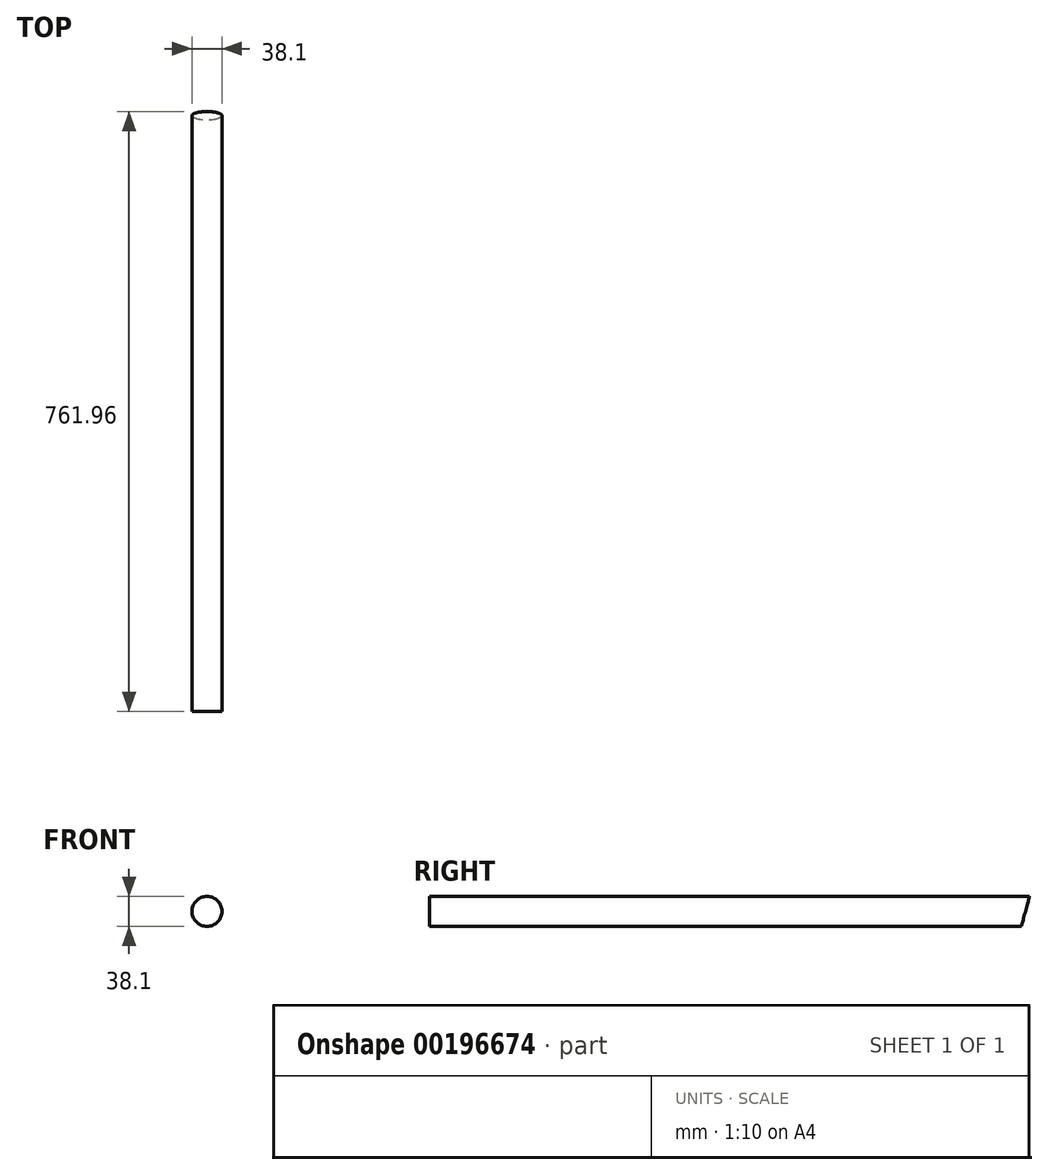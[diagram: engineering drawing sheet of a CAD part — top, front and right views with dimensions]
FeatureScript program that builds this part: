
annotation { "Feature Type Name" : "Feature", "Feature Type Description" : "" }
export const myFeature = defineFeature(function(context is Context, id is Id, definition is map)
    precondition{}
    {
        {
            var Q0;
            Q0=qCreatedBy(makeId("Front.planeOp"),FACE);
            var sketch = newSketch(context, id + "F0", { "sketchPlane" : qUnion([Q0])});
            skCircle(sketch, "E0", {"center": v(0, 0) * mm, "radius": 19.05 * mm});
            skSolve(sketch);
        }
        {
            var Q0;
            Q0=makeQuery(id+"F0.imprint","IMPRINT",FACE,{"disambiguationData":[TD([[makeQuery(id+"F0.imprint","IMPRINT",EDGE,{"derivedFrom":sQuery(id+"F0.wireOp",EDGE,"E0")}),1.0]])]});
            extrude(context, id + "F1", {"entities" : qUnion([Q0]), "depth" : 762 * mm});
        }
        {
            var Q0;
            Q0=qCreatedBy(makeId("Right.planeOp"),FACE);
            var sketch = newSketch(context, id + "F2", { "sketchPlane" : qUnion([Q0])});
            skLineSegment(sketch, "E1", {"start": v(0, -78.37) * mm, "end": v(0, 139.13) * mm});
            skLineSegment(sketch, "E2", {"start": v(0, 19.2) * mm, "end": v(-15.73, -39.51) * mm});
            skLineSegment(sketch, "E3", {"start": v(-15.73, -39.51) * mm, "end": v(0, -39.51) * mm});
            skSolve(sketch);
        }
        {
            var Q0;
            {var subQ0=sQuery(id+"F2.wireOp",EDGE,"E2");Q0=makeQuery(id+"F2.imprint","IMPRINT",FACE,{"disambiguationData":[TD([[makeQuery(id+"F2.imprint","IMPRINT",EDGE,{"derivedFrom":subQ0}),1.0]])]});}
            extrude(context, id + "F3", {"entities" : qUnion([Q0]), "operationType" : NewBodyOperationType.REMOVE, "oppositeDirection" : true, "depth" : 127 * mm, "hasSecondDirection" : true, "secondDirectionOppositeDirection" : false, "secondDirectionDepth" : 25.4 * mm});
        }
    });
